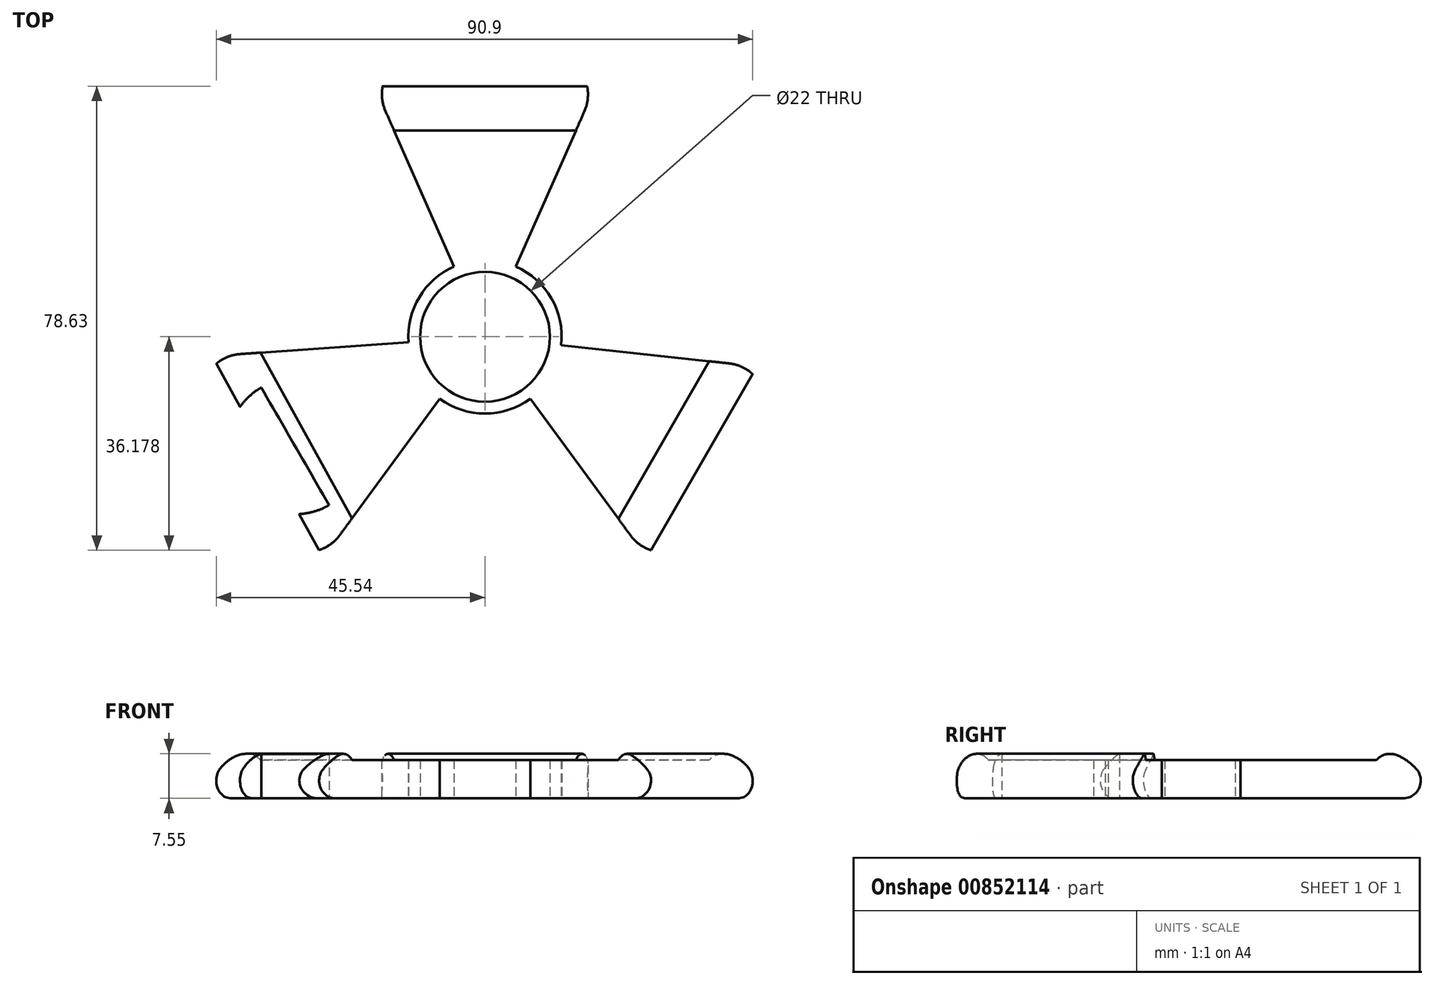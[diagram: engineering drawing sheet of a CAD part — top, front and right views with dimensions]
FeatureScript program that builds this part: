
annotation { "Feature Type Name" : "Feature", "Feature Type Description" : "" }
export const myFeature = defineFeature(function(context is Context, id is Id, definition is map)
    precondition{}
    {
        {
            var Q0;
            Q0=qCreatedBy(makeId("Top.planeOp"),FACE);
            var sketch = newSketch(context, id + "F0", { "sketchPlane" : qUnion([Q0])});
            skLineSegment(sketch, "E0", {"start": v(0, 55.7) * mm, "end": v(-32.16, 0) * mm});
            skLineSegment(sketch, "E1", {"start": v(-32.16, 0) * mm, "end": v(32.16, 0) * mm});
            skLineSegment(sketch, "E2", {"start": v(32.16, 0) * mm, "end": v(0, 55.7) * mm});
            skLineSegment(sketch, "E3", {"start": v(0, 55.7) * mm, "end": v(0, 0) * mm, "construction": true});
            skLineSegment(sketch, "E4", {"start": v(0, 0) * mm, "end": v(-32.16, 0) * mm, "construction": true});
            skLineSegment(sketch, "E5", {"start": v(-32.16, 0) * mm, "end": v(0, 18.57) * mm, "construction": true});
            skLineSegment(sketch, "E6", {"start": v(0, 18.57) * mm, "end": v(32.16, 0) * mm, "construction": true});
            skCircle(sketch, "E7", {"center": v(0, 18.57) * mm, "radius": 13 * mm});
            skCircle(sketch, "E8", {"center": v(-32.16, 0) * mm, "radius": 11.5 * mm});
            skCircle(sketch, "E9", {"center": v(0, 55.7) * mm, "radius": 6.79 * mm});
            skCircle(sketch, "E10", {"center": v(32.16, 0) * mm, "radius": 11.49 * mm});
            skLineSegment(sketch, "E11", {"start": v(0, 18.57) * mm, "end": v(-16.08, 27.85) * mm, "construction": true});
            skLineSegment(sketch, "E12", {"start": v(-16.08, 27.85) * mm, "end": v(0, 18.57) * mm, "construction": true});
            skLineSegment(sketch, "E13", {"start": v(0, 18.57) * mm, "end": v(16.08, 27.85) * mm, "construction": true});
            skLineSegment(sketch, "E14", {"start": v(6.79, 55.7) * mm, "end": v(-6.79, 55.7) * mm, "construction": true});
            skLineSegment(sketch, "E15", {"start": v(-20.66, 0) * mm, "end": v(-43.66, 0) * mm, "construction": true});
            skLineSegment(sketch, "E16", {"start": v(43.65, 0) * mm, "end": v(20.67, 0) * mm, "construction": true});
            skLineSegment(sketch, "E17", {"start": v(32.16, 0) * mm, "end": v(37.9, 9.95) * mm, "construction": true});
            skLineSegment(sketch, "E18", {"start": v(37.9, 9.95) * mm, "end": v(26.42, -9.95) * mm, "construction": true});
            skLineSegment(sketch, "E19", {"start": v(-32.16, 0) * mm, "end": v(-37.91, 9.96) * mm, "construction": true});
            skLineSegment(sketch, "E20", {"start": v(-37.91, 9.96) * mm, "end": v(-32.16, 0) * mm, "construction": true});
            skLineSegment(sketch, "E21", {"start": v(-32.16, 0) * mm, "end": v(-26.41, -9.96) * mm, "construction": true});
            skLineSegment(sketch, "E22", {"start": v(-26.41, -9.96) * mm, "end": v(0, 18.57) * mm});
            skLineSegment(sketch, "E23", {"start": v(-37.91, 9.96) * mm, "end": v(0, 18.57) * mm});
            skLineSegment(sketch, "E24", {"start": v(-6.79, 55.7) * mm, "end": v(0, 18.57) * mm});
            skLineSegment(sketch, "E25", {"start": v(6.79, 55.7) * mm, "end": v(0, 18.57) * mm});
            skLineSegment(sketch, "E26", {"start": v(26.42, -9.95) * mm, "end": v(0, 18.57) * mm});
            skLineSegment(sketch, "E27", {"start": v(37.9, 9.95) * mm, "end": v(0, 18.57) * mm});
            skLineSegment(sketch, "E28", {"start": v(32.16, 0) * mm, "end": v(41.84, 16.76) * mm});
            skLineSegment(sketch, "E29", {"start": v(41.84, 16.76) * mm, "end": v(22.49, -16.76) * mm});
            skLineSegment(sketch, "E30", {"start": v(-37.91, 9.96) * mm, "end": v(-21.6, -18.3) * mm});
            skLineSegment(sketch, "E31", {"start": v(-21.6, -18.3) * mm, "end": v(-37.91, 9.96) * mm});
            skLineSegment(sketch, "E32", {"start": v(-37.91, 9.96) * mm, "end": v(-42.88, 18.57) * mm});
            skLineSegment(sketch, "E33", {"start": v(6.79, 55.7) * mm, "end": v(19.36, 55.7) * mm});
            skLineSegment(sketch, "E34", {"start": v(19.36, 55.7) * mm, "end": v(-19.36, 55.7) * mm});
            skLineSegment(sketch, "E35", {"start": v(-42.88, 18.57) * mm, "end": v(0, 18.57) * mm});
            skLineSegment(sketch, "E36", {"start": v(0, 18.57) * mm, "end": v(-19.36, 55.7) * mm});
            skLineSegment(sketch, "E37", {"start": v(0, 18.57) * mm, "end": v(19.36, 55.7) * mm});
            skLineSegment(sketch, "E38", {"start": v(0, 18.57) * mm, "end": v(41.84, 16.76) * mm});
            skLineSegment(sketch, "E39", {"start": v(0, 18.57) * mm, "end": v(22.49, -16.76) * mm});
            skLineSegment(sketch, "E40", {"start": v(0, 18.57) * mm, "end": v(-21.6, -18.3) * mm});
            skLineSegment(sketch, "E41", {"start": v(-22.2, 5.75) * mm, "end": v(-42.12, -5.75) * mm, "construction": true});
            skLineSegment(sketch, "E42", {"start": v(32.16, 0) * mm, "end": v(42.1, -5.74) * mm, "construction": true});
            skLineSegment(sketch, "E43", {"start": v(0, 55.7) * mm, "end": v(0, 62.49) * mm, "construction": true});
            skLineSegment(sketch, "E44", {"start": v(-19.36, 55.7) * mm, "end": v(-19.36, 62.49) * mm, "construction": true});
            skLineSegment(sketch, "E45", {"start": v(-19.36, 62.49) * mm, "end": v(0, 62.49) * mm, "construction": true});
            skLineSegment(sketch, "E46", {"start": v(19.36, 62.49) * mm, "end": v(19.36, 55.7) * mm, "construction": true});
            skLineSegment(sketch, "E47", {"start": v(19.36, 62.49) * mm, "end": v(0, 62.49) * mm, "construction": true});
            skLineSegment(sketch, "E48", {"start": v(-42.88, 18.57) * mm, "end": v(-47.88, 15.2) * mm, "construction": true});
            skLineSegment(sketch, "E49", {"start": v(-47.88, 15.2) * mm, "end": v(-42.12, -5.75) * mm, "construction": true});
            skLineSegment(sketch, "E50", {"start": v(-21.6, -18.3) * mm, "end": v(-28.36, -20.16) * mm, "construction": true});
            skLineSegment(sketch, "E51", {"start": v(-28.36, -20.16) * mm, "end": v(-42.12, -5.75) * mm, "construction": true});
            skLineSegment(sketch, "E52", {"start": v(22.49, -16.76) * mm, "end": v(28.37, -20.15) * mm, "construction": true});
            skLineSegment(sketch, "E53", {"start": v(28.37, -20.15) * mm, "end": v(42.1, -5.74) * mm, "construction": true});
            skLineSegment(sketch, "E54", {"start": v(41.84, 16.76) * mm, "end": v(47.72, 13.36) * mm, "construction": true});
            skLineSegment(sketch, "E55", {"start": v(47.72, 13.36) * mm, "end": v(42.1, -5.74) * mm, "construction": true});
            skLineSegment(sketch, "E56", {"start": v(-28.36, -20.16) * mm, "end": v(0, 18.57) * mm});
            skLineSegment(sketch, "E57", {"start": v(0, 18.57) * mm, "end": v(-47.88, 15.2) * mm});
            skLineSegment(sketch, "E58", {"start": v(0, 18.57) * mm, "end": v(28.37, -20.15) * mm});
            skLineSegment(sketch, "E59", {"start": v(47.72, 13.36) * mm, "end": v(0, 18.57) * mm});
            skLineSegment(sketch, "E60", {"start": v(0, 18.57) * mm, "end": v(-19.36, 62.49) * mm});
            skLineSegment(sketch, "E61", {"start": v(0, 18.57) * mm, "end": v(19.36, 62.49) * mm});
            skLineSegment(sketch, "E62", {"start": v(19.36, 62.49) * mm, "end": v(-19.36, 62.49) * mm});
            skLineSegment(sketch, "E63", {"start": v(-28.36, -20.16) * mm, "end": v(-47.88, 15.2) * mm});
            skLineSegment(sketch, "E64", {"start": v(47.72, 13.36) * mm, "end": v(28.37, -20.15) * mm});
            skCircle(sketch, "E65", {"center": v(0, 18.57) * mm, "radius": 11 * mm});
            skLineSegment(sketch, "E66", {"start": v(0, 18.57) * mm, "end": v(-42.12, -5.75) * mm, "construction": true});
            skLineSegment(sketch, "E67", {"start": v(-16.37, 55.7) * mm, "end": v(-17.76, 52.64) * mm});
            skLineSegment(sketch, "E68", {"start": v(-16.89, 62.49) * mm, "end": v(-18.24, 59.93) * mm});
            skLineSegment(sketch, "E69", {"start": v(18.24, 59.95) * mm, "end": v(16.86, 62.49) * mm});
            skLineSegment(sketch, "E70", {"start": v(-45.13, 15.39) * mm, "end": v(-46.62, 12.91) * mm});
            skLineSegment(sketch, "E71", {"start": v(-26.71, -17.91) * mm, "end": v(-29.6, -17.91) * mm});
            skLineSegment(sketch, "E72", {"start": v(46.4, 11.1) * mm, "end": v(45.06, 13.65) * mm});
            skPoint(sketch, "E73.startSnap0", {"position": v(25.43, -18.46) * mm});
            skLineSegment(sketch, "E74", {"start": v(29.64, -17.95) * mm, "end": v(26.75, -17.95) * mm});
            skSolve(sketch);
        }
        {
            var Q0;
            {var subQ0=sQuery(id+"F0.wireOp",EDGE,"E23");var subQ1=sQuery(id+"F0.wireOp",EDGE,"E8");var subQ3=makeQuery(id+"F0.imprint","INTERSECT",VERTEX,{"derivedFrom":[subQ1,subQ0]});Q0=makeQuery(id+"F0.imprint","IMPRINT",FACE,{"disambiguationData":[TD([[makeQuery(id+"F0.imprint","IMPRINT",EDGE,{"disambiguationData":[TD([[subQ3,-1.0]])],"derivedFrom":subQ1}),1.0]])]});}
            var Q1;
            {var subQ0=sQuery(id+"F0.wireOp",EDGE,"E31");var subQ4=makeQuery(id+"F0.imprint","INTERSECT",VERTEX,{"derivedFrom":[sQuery(id+"F0.wireOp",EDGE,"E0"),sQuery(id+"F0.wireOp",EDGE,"E1"),subQ0]});Q1=makeQuery(id+"F0.imprint","IMPRINT",FACE,{"disambiguationData":[TD([[makeQuery(id+"F0.imprint","IMPRINT",EDGE,{"disambiguationData":[TD([[subQ4,1.0]])],"derivedFrom":subQ0}),1.0]])]});}
            var Q2;
            {var subQ0=sQuery(id+"F0.wireOp",EDGE,"E22");var subQ1=sQuery(id+"F0.wireOp",EDGE,"E8");var subQ3=makeQuery(id+"F0.imprint","INTERSECT",VERTEX,{"derivedFrom":[subQ1,subQ0]});Q2=makeQuery(id+"F0.imprint","IMPRINT",FACE,{"disambiguationData":[TD([[makeQuery(id+"F0.imprint","IMPRINT",EDGE,{"disambiguationData":[TD([[subQ3,1.0]])],"derivedFrom":subQ1}),1.0]])]});}
            var Q3;
            {var subQ0=sQuery(id+"F0.wireOp",EDGE,"E34");var subQ1=sQuery(id+"F0.wireOp",EDGE,"E9");var subQ2=makeQuery(id+"F0.imprint","INTERSECT",VERTEX,{"derivedFrom":[subQ1,sQuery(id+"F0.wireOp",EDGE,"E24"),subQ0]});Q3=makeQuery(id+"F0.imprint","IMPRINT",FACE,{"disambiguationData":[TD([[makeQuery(id+"F0.imprint","IMPRINT",EDGE,{"disambiguationData":[TD([[subQ2,1.0]])],"derivedFrom":subQ1}),1.0]])]});}
            var Q4;
            {var subQ0=sQuery(id+"F0.wireOp",EDGE,"E24");var subQ1=sQuery(id+"F0.wireOp",EDGE,"E9");var subQ3=makeQuery(id+"F0.imprint","INTERSECT",VERTEX,{"derivedFrom":[subQ1,subQ0]});Q4=makeQuery(id+"F0.imprint","IMPRINT",FACE,{"disambiguationData":[TD([[makeQuery(id+"F0.imprint","IMPRINT",EDGE,{"disambiguationData":[TD([[subQ3,1.0]])],"derivedFrom":subQ1}),1.0]])]});}
            var Q5;
            {var subQ0=sQuery(id+"F0.wireOp",EDGE,"E25");var subQ1=sQuery(id+"F0.wireOp",EDGE,"E9");var subQ3=makeQuery(id+"F0.imprint","INTERSECT",VERTEX,{"derivedFrom":[subQ1,subQ0]});Q5=makeQuery(id+"F0.imprint","IMPRINT",FACE,{"disambiguationData":[TD([[makeQuery(id+"F0.imprint","IMPRINT",EDGE,{"disambiguationData":[TD([[subQ3,-1.0]])],"derivedFrom":subQ1}),1.0]])]});}
            var Q6;
            {var subQ0=sQuery(id+"F0.wireOp",EDGE,"E27");var subQ1=sQuery(id+"F0.wireOp",EDGE,"E10");var subQ3=makeQuery(id+"F0.imprint","INTERSECT",VERTEX,{"derivedFrom":[subQ1,subQ0]});Q6=makeQuery(id+"F0.imprint","IMPRINT",FACE,{"disambiguationData":[TD([[makeQuery(id+"F0.imprint","IMPRINT",EDGE,{"disambiguationData":[TD([[subQ3,1.0]])],"derivedFrom":subQ1}),1.0]])]});}
            var Q7;
            {var subQ0=sQuery(id+"F0.wireOp",EDGE,"E26");var subQ1=sQuery(id+"F0.wireOp",EDGE,"E10");var subQ3=makeQuery(id+"F0.imprint","INTERSECT",VERTEX,{"derivedFrom":[subQ1,subQ0]});Q7=makeQuery(id+"F0.imprint","IMPRINT",FACE,{"disambiguationData":[TD([[makeQuery(id+"F0.imprint","IMPRINT",EDGE,{"disambiguationData":[TD([[subQ3,-1.0]])],"derivedFrom":subQ1}),1.0]])]});}
            var Q8;
            {var subQ0=sQuery(id+"F0.wireOp",EDGE,"E29");var subQ1=sQuery(id+"F0.wireOp",EDGE,"E10");var subQ2=makeQuery(id+"F0.imprint","INTERSECT",VERTEX,{"derivedFrom":[subQ1,sQuery(id+"F0.wireOp",EDGE,"E26"),subQ0]});Q8=makeQuery(id+"F0.imprint","IMPRINT",FACE,{"disambiguationData":[TD([[makeQuery(id+"F0.imprint","IMPRINT",EDGE,{"disambiguationData":[TD([[subQ2,-1.0]])],"derivedFrom":subQ1}),1.0]])]});}
            var Q9;
            {var subQ1=sQuery(id+"F0.wireOp",EDGE,"E0");var subQ3=sQuery(id+"F0.wireOp",EDGE,"E9");var subQ4=makeQuery(id+"F0.imprint","INTERSECT",VERTEX,{"derivedFrom":[subQ1,subQ3]});Q9=makeQuery(id+"F0.imprint","IMPRINT",FACE,{"disambiguationData":[TD([[makeQuery(id+"F0.imprint","IMPRINT",EDGE,{"disambiguationData":[TD([[subQ4,1.0]])],"derivedFrom":subQ3}),1.0]])]});}
            var Q10;
            {var subQ1=sQuery(id+"F0.wireOp",EDGE,"E0");var subQ3=sQuery(id+"F0.wireOp",EDGE,"E8");var subQ4=makeQuery(id+"F0.imprint","INTERSECT",VERTEX,{"derivedFrom":[subQ1,subQ3]});Q10=makeQuery(id+"F0.imprint","IMPRINT",FACE,{"disambiguationData":[TD([[makeQuery(id+"F0.imprint","IMPRINT",EDGE,{"disambiguationData":[TD([[subQ4,-1.0]])],"derivedFrom":subQ3}),1.0]])]});}
            var Q11;
            {var subQ1=sQuery(id+"F0.wireOp",EDGE,"E1");var subQ3=sQuery(id+"F0.wireOp",EDGE,"E8");var subQ4=makeQuery(id+"F0.imprint","INTERSECT",VERTEX,{"derivedFrom":[subQ1,subQ3]});Q11=makeQuery(id+"F0.imprint","IMPRINT",FACE,{"disambiguationData":[TD([[makeQuery(id+"F0.imprint","IMPRINT",EDGE,{"disambiguationData":[TD([[subQ4,1.0]])],"derivedFrom":subQ3}),1.0]])]});}
            var Q12;
            {var subQ1=sQuery(id+"F0.wireOp",EDGE,"E1");var subQ3=sQuery(id+"F0.wireOp",EDGE,"E10");var subQ4=makeQuery(id+"F0.imprint","INTERSECT",VERTEX,{"derivedFrom":[subQ1,subQ3]});Q12=makeQuery(id+"F0.imprint","IMPRINT",FACE,{"disambiguationData":[TD([[makeQuery(id+"F0.imprint","IMPRINT",EDGE,{"disambiguationData":[TD([[subQ4,-1.0]])],"derivedFrom":subQ3}),1.0]])]});}
            var Q13;
            {var subQ1=sQuery(id+"F0.wireOp",EDGE,"E2");var subQ3=sQuery(id+"F0.wireOp",EDGE,"E10");var subQ4=makeQuery(id+"F0.imprint","INTERSECT",VERTEX,{"derivedFrom":[subQ1,subQ3]});Q13=makeQuery(id+"F0.imprint","IMPRINT",FACE,{"disambiguationData":[TD([[makeQuery(id+"F0.imprint","IMPRINT",EDGE,{"disambiguationData":[TD([[subQ4,1.0]])],"derivedFrom":subQ3}),1.0]])]});}
            var Q14;
            {var subQ1=sQuery(id+"F0.wireOp",EDGE,"E2");var subQ3=sQuery(id+"F0.wireOp",EDGE,"E9");var subQ4=makeQuery(id+"F0.imprint","INTERSECT",VERTEX,{"derivedFrom":[subQ1,subQ3]});Q14=makeQuery(id+"F0.imprint","IMPRINT",FACE,{"disambiguationData":[TD([[makeQuery(id+"F0.imprint","IMPRINT",EDGE,{"disambiguationData":[TD([[subQ4,-1.0]])],"derivedFrom":subQ3}),1.0]])]});}
            var Q15;
            {var subQ1=sQuery(id+"F0.wireOp",EDGE,"E0");var subQ3=sQuery(id+"F0.wireOp",EDGE,"E8");var subQ4=makeQuery(id+"F0.imprint","INTERSECT",VERTEX,{"derivedFrom":[subQ1,subQ3]});Q15=makeQuery(id+"F0.imprint","IMPRINT",FACE,{"disambiguationData":[TD([[makeQuery(id+"F0.imprint","IMPRINT",EDGE,{"disambiguationData":[TD([[subQ4,1.0]])],"derivedFrom":subQ3}),1.0]])]});}
            var Q16;
            {var subQ0=sQuery(id+"F0.wireOp",EDGE,"E23");var subQ6=sQuery(id+"F0.wireOp",EDGE,"E0");var subQ11=makeQuery(id+"F0.imprint","INTERSECT",VERTEX,{"derivedFrom":[subQ6,subQ0]});Q16=makeQuery(id+"F0.imprint","IMPRINT",FACE,{"disambiguationData":[TD([[makeQuery(id+"F0.imprint","IMPRINT",EDGE,{"disambiguationData":[TD([[subQ11,-1.0]])],"derivedFrom":subQ6}),1.0]])]});}
            var Q17;
            {var subQ0=sQuery(id+"F0.wireOp",EDGE,"E23");var subQ1=sQuery(id+"F0.wireOp",EDGE,"E0");var subQ2=makeQuery(id+"F0.imprint","INTERSECT",VERTEX,{"derivedFrom":[subQ1,subQ0]});Q17=makeQuery(id+"F0.imprint","IMPRINT",FACE,{"disambiguationData":[TD([[makeQuery(id+"F0.imprint","IMPRINT",EDGE,{"disambiguationData":[TD([[subQ2,-1.0]])],"derivedFrom":subQ1}),-1.0]])]});}
            var Q18;
            {var subQ0=sQuery(id+"F0.wireOp",EDGE,"E8");var subQ1=sQuery(id+"F0.wireOp",EDGE,"E1");var subQ2=makeQuery(id+"F0.imprint","INTERSECT",VERTEX,{"derivedFrom":[subQ1,subQ0]});Q18=makeQuery(id+"F0.imprint","IMPRINT",FACE,{"disambiguationData":[TD([[makeQuery(id+"F0.imprint","IMPRINT",EDGE,{"disambiguationData":[TD([[subQ2,-1.0]])],"derivedFrom":subQ1}),-1.0]])]});}
            var Q19;
            {var subQ0=sQuery(id+"F0.wireOp",EDGE,"E26");var subQ9=sQuery(id+"F0.wireOp",EDGE,"E1");var subQ11=makeQuery(id+"F0.imprint","INTERSECT",VERTEX,{"derivedFrom":[subQ9,subQ0]});Q19=makeQuery(id+"F0.imprint","IMPRINT",FACE,{"disambiguationData":[TD([[makeQuery(id+"F0.imprint","IMPRINT",EDGE,{"disambiguationData":[TD([[subQ11,-1.0]])],"derivedFrom":subQ9}),1.0]])]});}
            var Q20;
            {var subQ1=sQuery(id+"F0.wireOp",EDGE,"E1");var subQ3=sQuery(id+"F0.wireOp",EDGE,"E10");var subQ4=makeQuery(id+"F0.imprint","INTERSECT",VERTEX,{"derivedFrom":[subQ1,subQ3]});Q20=makeQuery(id+"F0.imprint","IMPRINT",FACE,{"disambiguationData":[TD([[makeQuery(id+"F0.imprint","IMPRINT",EDGE,{"disambiguationData":[TD([[subQ4,1.0]])],"derivedFrom":subQ3}),1.0]])]});}
            var Q21;
            {var subQ0=sQuery(id+"F0.wireOp",EDGE,"E26");var subQ1=sQuery(id+"F0.wireOp",EDGE,"E1");var subQ2=makeQuery(id+"F0.imprint","INTERSECT",VERTEX,{"derivedFrom":[subQ1,subQ0]});Q21=makeQuery(id+"F0.imprint","IMPRINT",FACE,{"disambiguationData":[TD([[makeQuery(id+"F0.imprint","IMPRINT",EDGE,{"disambiguationData":[TD([[subQ2,-1.0]])],"derivedFrom":subQ1}),-1.0]])]});}
            var Q22;
            {var subQ0=sQuery(id+"F0.wireOp",EDGE,"E10");var subQ1=sQuery(id+"F0.wireOp",EDGE,"E2");var subQ2=makeQuery(id+"F0.imprint","INTERSECT",VERTEX,{"derivedFrom":[subQ1,subQ0]});Q22=makeQuery(id+"F0.imprint","IMPRINT",FACE,{"disambiguationData":[TD([[makeQuery(id+"F0.imprint","IMPRINT",EDGE,{"disambiguationData":[TD([[subQ2,-1.0]])],"derivedFrom":subQ1}),-1.0]])]});}
            var Q23;
            {var subQ1=sQuery(id+"F0.wireOp",EDGE,"E0");var subQ3=sQuery(id+"F0.wireOp",EDGE,"E9");var subQ4=makeQuery(id+"F0.imprint","INTERSECT",VERTEX,{"derivedFrom":[subQ1,subQ3]});Q23=makeQuery(id+"F0.imprint","IMPRINT",FACE,{"disambiguationData":[TD([[makeQuery(id+"F0.imprint","IMPRINT",EDGE,{"disambiguationData":[TD([[subQ4,-1.0]])],"derivedFrom":subQ3}),1.0]])]});}
            var Q24;
            {var subQ0=sQuery(id+"F0.wireOp",EDGE,"E25");var subQ1=sQuery(id+"F0.wireOp",EDGE,"E2");var subQ2=makeQuery(id+"F0.imprint","INTERSECT",VERTEX,{"derivedFrom":[subQ1,subQ0]});Q24=makeQuery(id+"F0.imprint","IMPRINT",FACE,{"disambiguationData":[TD([[makeQuery(id+"F0.imprint","IMPRINT",EDGE,{"disambiguationData":[TD([[subQ2,-1.0]])],"derivedFrom":subQ1}),-1.0]])]});}
            var Q25;
            {var subQ0=sQuery(id+"F0.wireOp",EDGE,"E9");var subQ1=sQuery(id+"F0.wireOp",EDGE,"E0");var subQ2=makeQuery(id+"F0.imprint","INTERSECT",VERTEX,{"derivedFrom":[subQ1,subQ0]});Q25=makeQuery(id+"F0.imprint","IMPRINT",FACE,{"disambiguationData":[TD([[makeQuery(id+"F0.imprint","IMPRINT",EDGE,{"disambiguationData":[TD([[subQ2,-1.0]])],"derivedFrom":subQ1}),-1.0]])]});}
            var Q26;
            {var subQ0=sQuery(id+"F0.wireOp",EDGE,"E9");var subQ1=sQuery(id+"F0.wireOp",EDGE,"E0");var subQ2=makeQuery(id+"F0.imprint","INTERSECT",VERTEX,{"derivedFrom":[subQ1,subQ0]});Q26=makeQuery(id+"F0.imprint","IMPRINT",FACE,{"disambiguationData":[TD([[makeQuery(id+"F0.imprint","IMPRINT",EDGE,{"disambiguationData":[TD([[subQ2,-1.0]])],"derivedFrom":subQ1}),1.0]])]});}
            var Q27;
            {var subQ0=sQuery(id+"F0.wireOp",EDGE,"E25");var subQ1=sQuery(id+"F0.wireOp",EDGE,"E7");var subQ2=makeQuery(id+"F0.imprint","INTERSECT",VERTEX,{"derivedFrom":[subQ1,subQ0]});Q27=makeQuery(id+"F0.imprint","IMPRINT",FACE,{"disambiguationData":[TD([[makeQuery(id+"F0.imprint","IMPRINT",EDGE,{"disambiguationData":[TD([[subQ2,1.0]])],"derivedFrom":subQ1}),1.0]])]});}
            var Q28;
            {var subQ0=sQuery(id+"F0.wireOp",EDGE,"E25");var subQ1=sQuery(id+"F0.wireOp",EDGE,"E7");var subQ2=makeQuery(id+"F0.imprint","INTERSECT",VERTEX,{"derivedFrom":[subQ1,subQ0]});Q28=makeQuery(id+"F0.imprint","IMPRINT",FACE,{"disambiguationData":[TD([[makeQuery(id+"F0.imprint","IMPRINT",EDGE,{"disambiguationData":[TD([[subQ2,-1.0]])],"derivedFrom":subQ1}),1.0]])]});}
            var Q29;
            {var subQ0=sQuery(id+"F0.wireOp",EDGE,"E24");var subQ1=sQuery(id+"F0.wireOp",EDGE,"E7");var subQ2=makeQuery(id+"F0.imprint","INTERSECT",VERTEX,{"derivedFrom":[subQ1,subQ0]});Q29=makeQuery(id+"F0.imprint","IMPRINT",FACE,{"disambiguationData":[TD([[makeQuery(id+"F0.imprint","IMPRINT",EDGE,{"disambiguationData":[TD([[subQ2,-1.0]])],"derivedFrom":subQ1}),1.0]])]});}
            var Q30;
            {var subQ0=sQuery(id+"F0.wireOp",EDGE,"E23");var subQ1=sQuery(id+"F0.wireOp",EDGE,"E7");var subQ2=makeQuery(id+"F0.imprint","INTERSECT",VERTEX,{"derivedFrom":[subQ1,subQ0]});Q30=makeQuery(id+"F0.imprint","IMPRINT",FACE,{"disambiguationData":[TD([[makeQuery(id+"F0.imprint","IMPRINT",EDGE,{"disambiguationData":[TD([[subQ2,-1.0]])],"derivedFrom":subQ1}),1.0]])]});}
            var Q31;
            {var subQ0=sQuery(id+"F0.wireOp",EDGE,"E22");var subQ1=sQuery(id+"F0.wireOp",EDGE,"E7");var subQ2=makeQuery(id+"F0.imprint","INTERSECT",VERTEX,{"derivedFrom":[subQ1,subQ0]});Q31=makeQuery(id+"F0.imprint","IMPRINT",FACE,{"disambiguationData":[TD([[makeQuery(id+"F0.imprint","IMPRINT",EDGE,{"disambiguationData":[TD([[subQ2,-1.0]])],"derivedFrom":subQ1}),1.0]])]});}
            var Q32;
            {var subQ0=sQuery(id+"F0.wireOp",EDGE,"E26");var subQ1=sQuery(id+"F0.wireOp",EDGE,"E7");var subQ2=makeQuery(id+"F0.imprint","INTERSECT",VERTEX,{"derivedFrom":[subQ1,subQ0]});Q32=makeQuery(id+"F0.imprint","IMPRINT",FACE,{"disambiguationData":[TD([[makeQuery(id+"F0.imprint","IMPRINT",EDGE,{"disambiguationData":[TD([[subQ2,-1.0]])],"derivedFrom":subQ1}),1.0]])]});}
            var Q33;
            {var subQ0=sQuery(id+"F0.wireOp",EDGE,"E27");var subQ1=sQuery(id+"F0.wireOp",EDGE,"E7");var subQ2=makeQuery(id+"F0.imprint","INTERSECT",VERTEX,{"derivedFrom":[subQ1,subQ0]});Q33=makeQuery(id+"F0.imprint","IMPRINT",FACE,{"disambiguationData":[TD([[makeQuery(id+"F0.imprint","IMPRINT",EDGE,{"disambiguationData":[TD([[subQ2,-1.0]])],"derivedFrom":subQ1}),1.0]])]});}
            var Q34;
            {var subQ1=sQuery(id+"F0.wireOp",EDGE,"E22");var subQ6=sQuery(id+"F0.wireOp",EDGE,"E1");var subQ7=makeQuery(id+"F0.imprint","INTERSECT",VERTEX,{"derivedFrom":[subQ6,subQ1]});Q34=makeQuery(id+"F0.imprint","IMPRINT",FACE,{"disambiguationData":[TD([[makeQuery(id+"F0.imprint","IMPRINT",EDGE,{"disambiguationData":[TD([[subQ7,-1.0]])],"derivedFrom":subQ6}),-1.0]])]});}
            var Q35;
            {var subQ0=sQuery(id+"F0.wireOp",EDGE,"E22");var subQ1=sQuery(id+"F0.wireOp",EDGE,"E1");var subQ2=makeQuery(id+"F0.imprint","INTERSECT",VERTEX,{"derivedFrom":[subQ1,subQ0]});Q35=makeQuery(id+"F0.imprint","IMPRINT",FACE,{"disambiguationData":[TD([[makeQuery(id+"F0.imprint","IMPRINT",EDGE,{"disambiguationData":[TD([[subQ2,-1.0]])],"derivedFrom":subQ1}),1.0]])]});}
            var Q36;
            {var subQ4=sQuery(id+"F0.wireOp",EDGE,"E57");var subQ7=sQuery(id+"F0.wireOp",EDGE,"E0");var subQ9=makeQuery(id+"F0.imprint","INTERSECT",VERTEX,{"derivedFrom":[subQ7,subQ4]});Q36=makeQuery(id+"F0.imprint","IMPRINT",FACE,{"disambiguationData":[TD([[makeQuery(id+"F0.imprint","IMPRINT",EDGE,{"disambiguationData":[TD([[subQ9,-1.0]])],"derivedFrom":subQ7}),-1.0]])]});}
            var Q37;
            {var subQ1=sQuery(id+"F0.wireOp",EDGE,"E1");var subQ7=sQuery(id+"F0.wireOp",EDGE,"E58");var subQ9=makeQuery(id+"F0.imprint","INTERSECT",VERTEX,{"derivedFrom":[subQ1,subQ7]});Q37=makeQuery(id+"F0.imprint","IMPRINT",FACE,{"disambiguationData":[TD([[makeQuery(id+"F0.imprint","IMPRINT",EDGE,{"disambiguationData":[TD([[subQ9,-1.0]])],"derivedFrom":subQ1}),-1.0]])]});}
            var Q38;
            {var subQ1=sQuery(id+"F0.wireOp",EDGE,"E27");var subQ6=sQuery(id+"F0.wireOp",EDGE,"E2");var subQ7=makeQuery(id+"F0.imprint","INTERSECT",VERTEX,{"derivedFrom":[subQ6,subQ1]});Q38=makeQuery(id+"F0.imprint","IMPRINT",FACE,{"disambiguationData":[TD([[makeQuery(id+"F0.imprint","IMPRINT",EDGE,{"disambiguationData":[TD([[subQ7,-1.0]])],"derivedFrom":subQ6}),-1.0]])]});}
            var Q39;
            {var subQ0=sQuery(id+"F0.wireOp",EDGE,"E61");var subQ1=sQuery(id+"F0.wireOp",EDGE,"E2");var subQ2=makeQuery(id+"F0.imprint","INTERSECT",VERTEX,{"derivedFrom":[subQ1,subQ0]});Q39=makeQuery(id+"F0.imprint","IMPRINT",FACE,{"disambiguationData":[TD([[makeQuery(id+"F0.imprint","IMPRINT",EDGE,{"disambiguationData":[TD([[subQ2,-1.0]])],"derivedFrom":subQ1}),1.0]])]});}
            var Q40;
            {var subQ0=sQuery(id+"F0.wireOp",EDGE,"E24");var subQ1=sQuery(id+"F0.wireOp",EDGE,"E0");var subQ2=makeQuery(id+"F0.imprint","INTERSECT",VERTEX,{"derivedFrom":[subQ1,subQ0]});Q40=makeQuery(id+"F0.imprint","IMPRINT",FACE,{"disambiguationData":[TD([[makeQuery(id+"F0.imprint","IMPRINT",EDGE,{"disambiguationData":[TD([[subQ2,-1.0]])],"derivedFrom":subQ1}),1.0]])]});}
            var Q41;
            {var subQ1=sQuery(id+"F0.wireOp",EDGE,"E24");var subQ6=sQuery(id+"F0.wireOp",EDGE,"E0");var subQ7=makeQuery(id+"F0.imprint","INTERSECT",VERTEX,{"derivedFrom":[subQ6,subQ1]});Q41=makeQuery(id+"F0.imprint","IMPRINT",FACE,{"disambiguationData":[TD([[makeQuery(id+"F0.imprint","IMPRINT",EDGE,{"disambiguationData":[TD([[subQ7,-1.0]])],"derivedFrom":subQ6}),-1.0]])]});}
            var Q42;
            {var subQ4=sQuery(id+"F0.wireOp",EDGE,"E61");var subQ7=sQuery(id+"F0.wireOp",EDGE,"E2");var subQ9=makeQuery(id+"F0.imprint","INTERSECT",VERTEX,{"derivedFrom":[subQ7,subQ4]});Q42=makeQuery(id+"F0.imprint","IMPRINT",FACE,{"disambiguationData":[TD([[makeQuery(id+"F0.imprint","IMPRINT",EDGE,{"disambiguationData":[TD([[subQ9,-1.0]])],"derivedFrom":subQ7}),-1.0]])]});}
            var Q43;
            {var subQ0=sQuery(id+"F0.wireOp",EDGE,"E27");var subQ1=sQuery(id+"F0.wireOp",EDGE,"E2");var subQ2=makeQuery(id+"F0.imprint","INTERSECT",VERTEX,{"derivedFrom":[subQ1,subQ0]});Q43=makeQuery(id+"F0.imprint","IMPRINT",FACE,{"disambiguationData":[TD([[makeQuery(id+"F0.imprint","IMPRINT",EDGE,{"disambiguationData":[TD([[subQ2,-1.0]])],"derivedFrom":subQ1}),1.0]])]});}
            var Q44;
            {var subQ0=sQuery(id+"F0.wireOp",EDGE,"E58");var subQ1=sQuery(id+"F0.wireOp",EDGE,"E1");var subQ2=makeQuery(id+"F0.imprint","INTERSECT",VERTEX,{"derivedFrom":[subQ1,subQ0]});Q44=makeQuery(id+"F0.imprint","IMPRINT",FACE,{"disambiguationData":[TD([[makeQuery(id+"F0.imprint","IMPRINT",EDGE,{"disambiguationData":[TD([[subQ2,-1.0]])],"derivedFrom":subQ1}),1.0]])]});}
            var Q45;
            {var subQ0=sQuery(id+"F0.wireOp",EDGE,"E57");var subQ1=sQuery(id+"F0.wireOp",EDGE,"E0");var subQ2=makeQuery(id+"F0.imprint","INTERSECT",VERTEX,{"derivedFrom":[subQ1,subQ0]});Q45=makeQuery(id+"F0.imprint","IMPRINT",FACE,{"disambiguationData":[TD([[makeQuery(id+"F0.imprint","IMPRINT",EDGE,{"disambiguationData":[TD([[subQ2,-1.0]])],"derivedFrom":subQ1}),1.0]])]});}
            var Q46;
            {var subQ0=sQuery(id+"F0.wireOp",EDGE,"E57");var subQ1=sQuery(id+"F0.wireOp",EDGE,"E7");var subQ2=makeQuery(id+"F0.imprint","INTERSECT",VERTEX,{"derivedFrom":[subQ1,subQ0]});Q46=makeQuery(id+"F0.imprint","IMPRINT",FACE,{"disambiguationData":[TD([[makeQuery(id+"F0.imprint","IMPRINT",EDGE,{"disambiguationData":[TD([[subQ2,-1.0]])],"derivedFrom":subQ1}),1.0]])]});}
            var Q47;
            {var subQ0=sQuery(id+"F0.wireOp",EDGE,"E40");var subQ1=sQuery(id+"F0.wireOp",EDGE,"E7");var subQ2=makeQuery(id+"F0.imprint","INTERSECT",VERTEX,{"derivedFrom":[subQ1,subQ0]});Q47=makeQuery(id+"F0.imprint","IMPRINT",FACE,{"disambiguationData":[TD([[makeQuery(id+"F0.imprint","IMPRINT",EDGE,{"disambiguationData":[TD([[subQ2,-1.0]])],"derivedFrom":subQ1}),1.0]])]});}
            var Q48;
            {var subQ0=sQuery(id+"F0.wireOp",EDGE,"E37");var subQ1=sQuery(id+"F0.wireOp",EDGE,"E7");var subQ2=makeQuery(id+"F0.imprint","INTERSECT",VERTEX,{"derivedFrom":[subQ1,subQ0]});Q48=makeQuery(id+"F0.imprint","IMPRINT",FACE,{"disambiguationData":[TD([[makeQuery(id+"F0.imprint","IMPRINT",EDGE,{"disambiguationData":[TD([[subQ2,1.0]])],"derivedFrom":subQ1}),1.0]])]});}
            var Q49;
            {var subQ0=sQuery(id+"F0.wireOp",EDGE,"E36");var subQ1=sQuery(id+"F0.wireOp",EDGE,"E7");var subQ2=makeQuery(id+"F0.imprint","INTERSECT",VERTEX,{"derivedFrom":[subQ1,subQ0]});Q49=makeQuery(id+"F0.imprint","IMPRINT",FACE,{"disambiguationData":[TD([[makeQuery(id+"F0.imprint","IMPRINT",EDGE,{"disambiguationData":[TD([[subQ2,-1.0]])],"derivedFrom":subQ1}),1.0]])]});}
            var Q50;
            {var subQ0=sQuery(id+"F0.wireOp",EDGE,"E35");var subQ1=sQuery(id+"F0.wireOp",EDGE,"E7");var subQ2=makeQuery(id+"F0.imprint","INTERSECT",VERTEX,{"derivedFrom":[subQ1,subQ0]});Q50=makeQuery(id+"F0.imprint","IMPRINT",FACE,{"disambiguationData":[TD([[makeQuery(id+"F0.imprint","IMPRINT",EDGE,{"disambiguationData":[TD([[subQ2,-1.0]])],"derivedFrom":subQ1}),1.0]])]});}
            var Q51;
            {var subQ0=sQuery(id+"F0.wireOp",EDGE,"E56");var subQ1=sQuery(id+"F0.wireOp",EDGE,"E7");var subQ2=makeQuery(id+"F0.imprint","INTERSECT",VERTEX,{"derivedFrom":[subQ1,subQ0]});Q51=makeQuery(id+"F0.imprint","IMPRINT",FACE,{"disambiguationData":[TD([[makeQuery(id+"F0.imprint","IMPRINT",EDGE,{"disambiguationData":[TD([[subQ2,-1.0]])],"derivedFrom":subQ1}),1.0]])]});}
            var Q52;
            {var subQ0=sQuery(id+"F0.wireOp",EDGE,"E59");var subQ1=sQuery(id+"F0.wireOp",EDGE,"E7");var subQ2=makeQuery(id+"F0.imprint","INTERSECT",VERTEX,{"derivedFrom":[subQ1,subQ0]});Q52=makeQuery(id+"F0.imprint","IMPRINT",FACE,{"disambiguationData":[TD([[makeQuery(id+"F0.imprint","IMPRINT",EDGE,{"disambiguationData":[TD([[subQ2,-1.0]])],"derivedFrom":subQ1}),1.0]])]});}
            var Q53;
            {var subQ0=sQuery(id+"F0.wireOp",EDGE,"E61");var subQ1=sQuery(id+"F0.wireOp",EDGE,"E7");var subQ2=makeQuery(id+"F0.imprint","INTERSECT",VERTEX,{"derivedFrom":[subQ1,subQ0]});Q53=makeQuery(id+"F0.imprint","IMPRINT",FACE,{"disambiguationData":[TD([[makeQuery(id+"F0.imprint","IMPRINT",EDGE,{"disambiguationData":[TD([[subQ2,1.0]])],"derivedFrom":subQ1}),1.0]])]});}
            var Q54;
            {var subQ0=sQuery(id+"F0.wireOp",EDGE,"E58");var subQ1=sQuery(id+"F0.wireOp",EDGE,"E7");var subQ2=makeQuery(id+"F0.imprint","INTERSECT",VERTEX,{"derivedFrom":[subQ1,subQ0]});Q54=makeQuery(id+"F0.imprint","IMPRINT",FACE,{"disambiguationData":[TD([[makeQuery(id+"F0.imprint","IMPRINT",EDGE,{"disambiguationData":[TD([[subQ2,-1.0]])],"derivedFrom":subQ1}),1.0]])]});}
            var Q55;
            {var subQ0=sQuery(id+"F0.wireOp",EDGE,"E39");var subQ1=sQuery(id+"F0.wireOp",EDGE,"E7");var subQ2=makeQuery(id+"F0.imprint","INTERSECT",VERTEX,{"derivedFrom":[subQ1,subQ0]});Q55=makeQuery(id+"F0.imprint","IMPRINT",FACE,{"disambiguationData":[TD([[makeQuery(id+"F0.imprint","IMPRINT",EDGE,{"disambiguationData":[TD([[subQ2,-1.0]])],"derivedFrom":subQ1}),1.0]])]});}
            var Q56;
            {var subQ0=sQuery(id+"F0.wireOp",EDGE,"E60");var subQ1=sQuery(id+"F0.wireOp",EDGE,"E7");var subQ2=makeQuery(id+"F0.imprint","INTERSECT",VERTEX,{"derivedFrom":[subQ1,subQ0]});Q56=makeQuery(id+"F0.imprint","IMPRINT",FACE,{"disambiguationData":[TD([[makeQuery(id+"F0.imprint","IMPRINT",EDGE,{"disambiguationData":[TD([[subQ2,-1.0]])],"derivedFrom":subQ1}),1.0]])]});}
            var Q57;
            {var subQ0=sQuery(id+"F0.wireOp",EDGE,"E68");Q57=makeQuery(id+"F0.imprint","IMPRINT",FACE,{"disambiguationData":[TD([[makeQuery(id+"F0.imprint","IMPRINT",EDGE,{"derivedFrom":subQ0}),1.0]])]});}
            var Q58;
            {var subQ0=sQuery(id+"F0.wireOp",EDGE,"E70");Q58=makeQuery(id+"F0.imprint","IMPRINT",FACE,{"disambiguationData":[TD([[makeQuery(id+"F0.imprint","IMPRINT",EDGE,{"derivedFrom":subQ0}),1.0]])]});}
            var Q59;
            {var subQ0=sQuery(id+"F0.wireOp",EDGE,"E71");Q59=makeQuery(id+"F0.imprint","IMPRINT",FACE,{"disambiguationData":[TD([[makeQuery(id+"F0.imprint","IMPRINT",EDGE,{"derivedFrom":subQ0}),-1.0]])]});}
            var Q60;
            {var subQ0=sQuery(id+"F0.wireOp",EDGE,"E72");Q60=makeQuery(id+"F0.imprint","IMPRINT",FACE,{"disambiguationData":[TD([[makeQuery(id+"F0.imprint","IMPRINT",EDGE,{"derivedFrom":subQ0}),1.0]])]});}
            var Q61;
            {var subQ0=sQuery(id+"F0.wireOp",EDGE,"E74");Q61=makeQuery(id+"F0.imprint","IMPRINT",FACE,{"disambiguationData":[TD([[makeQuery(id+"F0.imprint","IMPRINT",EDGE,{"derivedFrom":subQ0}),-1.0]])]});}
            var Q62;
            {var subQ0=sQuery(id+"F0.wireOp",EDGE,"E69");Q62=makeQuery(id+"F0.imprint","IMPRINT",FACE,{"disambiguationData":[TD([[makeQuery(id+"F0.imprint","IMPRINT",EDGE,{"derivedFrom":subQ0}),1.0]])]});}
            extrude(context, id + "F1", {"entities" : qUnion([Q0, Q1, Q2, Q3, Q4, Q5, Q6, Q7, Q8, Q9, Q10, Q11, Q12, Q13, Q14, Q15, Q16, Q17, Q18, Q19, Q20, Q21, Q22, Q23, Q24, Q25, Q26, Q27, Q28, Q29, Q30, Q31, Q32, Q33, Q34, Q35, Q36, Q37, Q38, Q39, Q40, Q41, Q42, Q43, Q44, Q45, Q46, Q47, Q48, Q49, Q50, Q51, Q52, Q53, Q54, Q55, Q56, Q57, Q58, Q59, Q60, Q61, Q62]), "depth" : 8 * mm, "offsetDistance" : 25 * mm});
        }
        {
            var Q0;
            Q0=makeQuery(id+"F1.opExtrude","CAP_EDGE",EDGE,{"disambiguationData":[OSD([sQuery(id+"F0.wireOp",EDGE,"E63")])],"isStart":false});
            var Q1;
            Q1=makeQuery(id+"F1.opExtrude","CAP_EDGE",EDGE,{"disambiguationData":[OSD([sQuery(id+"F0.wireOp",EDGE,"E64")])],"isStart":false});
            var Q2;
            Q2=makeQuery(id+"F1.opExtrude","CAP_EDGE",EDGE,{"disambiguationData":[OSD([sQuery(id+"F0.wireOp",EDGE,"E62")])],"isStart":false});
            fillet(context, id + "F2", {"entities" : qUnion([Q0, Q1, Q2]), "radius" : 9 * mm, "tangentPropagation" : true, "allowEdgeOverflow" : false});
        }
        {
            var Q0;
            Q0=makeQuery(id+"F1.opExtrude","CAP_FACE",FACE,{"disambiguationData":[OSD([sQuery(id+"F0.wireOp",EDGE,"E7"),sQuery(id+"F0.wireOp",EDGE,"E56"),sQuery(id+"F0.wireOp",EDGE,"E57"),sQuery(id+"F0.wireOp",EDGE,"E58"),sQuery(id+"F0.wireOp",EDGE,"E59"),sQuery(id+"F0.wireOp",EDGE,"E60"),sQuery(id+"F0.wireOp",EDGE,"E61"),sQuery(id+"F0.wireOp",EDGE,"E62"),sQuery(id+"F0.wireOp",EDGE,"E63"),sQuery(id+"F0.wireOp",EDGE,"E64")])],"isStart":false});
            var sketch = newSketch(context, id + "F3", { "sketchPlane" : qUnion([Q0])});
            skSolve(sketch);
        }
        {
            var Q0;
            Q0 = qSketchRegion(id + "F3", true);
            var Q1;
            {var subQ8=sQuery(id+"F0.wireOp",EDGE,"E56");Q1=makeQuery(id+"F3.imprint","IMPRINT",FACE,{"disambiguationData":[TD([[makeQuery(id+"F3.imprint","IMPRINT",EDGE,{"derivedFrom":makeQuery(id+"F1.opExtrude","CAP_EDGE",EDGE,{"disambiguationData":[OSD([subQ8])],"isStart":false})}),1.0]])]});}
            extrude(context, id + "F4", {"entities" : qUnion([Q0, Q1]), "operationType" : NewBodyOperationType.REMOVE, "oppositeDirection" : true, "depth" : 1.5 * mm, "offsetDistance" : 25 * mm});
        }
        {
            var Q0;
            {var subQ0=sQuery(id+"F0.wireOp",EDGE,"E64");var subQ1=sQuery(id+"F0.wireOp",EDGE,"E63");var subQ2=sQuery(id+"F0.wireOp",EDGE,"E62");var subQ3=sQuery(id+"F0.wireOp",EDGE,"E61");var subQ4=sQuery(id+"F0.wireOp",EDGE,"E60");var subQ5=sQuery(id+"F0.wireOp",EDGE,"E59");var subQ6=sQuery(id+"F0.wireOp",EDGE,"E58");var subQ7=sQuery(id+"F0.wireOp",EDGE,"E57");var subQ8=sQuery(id+"F0.wireOp",EDGE,"E56");var subQ9=sQuery(id+"F0.wireOp",EDGE,"E7");var subQ10=makeQuery(id+"F2.opFillet","BLEND_EDGE",EDGE,{"blendedFrom":[makeQuery(id+"F1.opExtrude","CAP_EDGE",EDGE,{"disambiguationData":[OSD([subQ0])],"isStart":false}),makeQuery(id+"F1.opExtrude","CAP_FACE",FACE,{"disambiguationData":[OSD([subQ9,subQ8,subQ7,subQ6,subQ5,subQ4,subQ3,subQ2,subQ1,subQ0])],"isStart":false})],"blendedInto":[makeQuery(id+"F1.opExtrude","CAP_FACE",FACE,{"disambiguationData":[OSD([subQ9,subQ8,subQ7,subQ6,subQ5,subQ4,subQ3,subQ2,subQ1,subQ0])],"isStart":false})]});Q0=makeQuery(id+"F4.boolean.opBoolean","MERGE",EDGE,{"derivedFrom":[subQ10,makeQuery(id+"F4.opExtrude","CAP_EDGE",EDGE,{"disambiguationData":[OSD([subQ9,subQ8,subQ7,subQ6,subQ5,subQ4,subQ3,subQ2,subQ1,subQ0]),TDD([makeQuery(id+"F3.imprint","IMPRINT",EDGE,{"derivedFrom":subQ10})])],"isStart":true})]});}
            var Q1;
            {var subQ0=sQuery(id+"F0.wireOp",EDGE,"E64");var subQ1=sQuery(id+"F0.wireOp",EDGE,"E63");var subQ2=sQuery(id+"F0.wireOp",EDGE,"E62");var subQ3=sQuery(id+"F0.wireOp",EDGE,"E61");var subQ4=sQuery(id+"F0.wireOp",EDGE,"E60");var subQ5=sQuery(id+"F0.wireOp",EDGE,"E59");var subQ6=sQuery(id+"F0.wireOp",EDGE,"E58");var subQ7=sQuery(id+"F0.wireOp",EDGE,"E57");var subQ8=sQuery(id+"F0.wireOp",EDGE,"E56");var subQ9=sQuery(id+"F0.wireOp",EDGE,"E7");var subQ10=makeQuery(id+"F2.opFillet","BLEND_EDGE",EDGE,{"blendedFrom":[makeQuery(id+"F1.opExtrude","CAP_EDGE",EDGE,{"disambiguationData":[OSD([subQ2])],"isStart":false}),makeQuery(id+"F1.opExtrude","CAP_FACE",FACE,{"disambiguationData":[OSD([subQ9,subQ8,subQ7,subQ6,subQ5,subQ4,subQ3,subQ2,subQ1,subQ0])],"isStart":false})],"blendedInto":[makeQuery(id+"F1.opExtrude","CAP_FACE",FACE,{"disambiguationData":[OSD([subQ9,subQ8,subQ7,subQ6,subQ5,subQ4,subQ3,subQ2,subQ1,subQ0])],"isStart":false})]});Q1=makeQuery(id+"F4.boolean.opBoolean","MERGE",EDGE,{"derivedFrom":[subQ10,makeQuery(id+"F4.opExtrude","CAP_EDGE",EDGE,{"disambiguationData":[OSD([subQ9,subQ8,subQ7,subQ6,subQ5,subQ4,subQ3,subQ2,subQ1,subQ0]),TDD([makeQuery(id+"F3.imprint","IMPRINT",EDGE,{"derivedFrom":subQ10})])],"isStart":true})]});}
            var Q2;
            {var subQ0=sQuery(id+"F0.wireOp",EDGE,"E64");var subQ1=sQuery(id+"F0.wireOp",EDGE,"E63");var subQ2=sQuery(id+"F0.wireOp",EDGE,"E62");var subQ3=sQuery(id+"F0.wireOp",EDGE,"E61");var subQ4=sQuery(id+"F0.wireOp",EDGE,"E60");var subQ5=sQuery(id+"F0.wireOp",EDGE,"E59");var subQ6=sQuery(id+"F0.wireOp",EDGE,"E58");var subQ7=sQuery(id+"F0.wireOp",EDGE,"E57");var subQ8=sQuery(id+"F0.wireOp",EDGE,"E56");var subQ9=sQuery(id+"F0.wireOp",EDGE,"E7");var subQ10=makeQuery(id+"F2.opFillet","BLEND_EDGE",EDGE,{"blendedFrom":[makeQuery(id+"F1.opExtrude","CAP_EDGE",EDGE,{"disambiguationData":[OSD([subQ1])],"isStart":false}),makeQuery(id+"F1.opExtrude","CAP_FACE",FACE,{"disambiguationData":[OSD([subQ9,subQ8,subQ7,subQ6,subQ5,subQ4,subQ3,subQ2,subQ1,subQ0])],"isStart":false})],"blendedInto":[makeQuery(id+"F1.opExtrude","CAP_FACE",FACE,{"disambiguationData":[OSD([subQ9,subQ8,subQ7,subQ6,subQ5,subQ4,subQ3,subQ2,subQ1,subQ0])],"isStart":false})]});Q2=makeQuery(id+"F4.boolean.opBoolean","MERGE",EDGE,{"derivedFrom":[subQ10,makeQuery(id+"F4.opExtrude","CAP_EDGE",EDGE,{"disambiguationData":[OSD([subQ9,subQ8,subQ7,subQ6,subQ5,subQ4,subQ3,subQ2,subQ1,subQ0]),TDD([makeQuery(id+"F3.imprint","IMPRINT",EDGE,{"derivedFrom":subQ10})])],"isStart":true})]});}
            var Q3;
            {var subQ0=sQuery(id+"F0.wireOp",EDGE,"E63");Q3=makeQuery(id+"F2.opFillet","BLEND_EDGE",EDGE,{"blendedFrom":[makeQuery(id+"F1.opExtrude","CAP_EDGE",EDGE,{"disambiguationData":[OSD([subQ0])],"isStart":false}),makeQuery(id+"F1.opExtrude","CAP_FACE",FACE,{"disambiguationData":[OSD([sQuery(id+"F0.wireOp",EDGE,"E7"),sQuery(id+"F0.wireOp",EDGE,"E56"),sQuery(id+"F0.wireOp",EDGE,"E57"),sQuery(id+"F0.wireOp",EDGE,"E58"),sQuery(id+"F0.wireOp",EDGE,"E59"),sQuery(id+"F0.wireOp",EDGE,"E60"),sQuery(id+"F0.wireOp",EDGE,"E61"),sQuery(id+"F0.wireOp",EDGE,"E62"),subQ0,sQuery(id+"F0.wireOp",EDGE,"E64"),sQuery(id+"F0.wireOp",EDGE,"E65"),sQuery(id+"F0.wireOp",EDGE,"E68"),sQuery(id+"F0.wireOp",EDGE,"E69"),sQuery(id+"F0.wireOp",EDGE,"E70"),sQuery(id+"F0.wireOp",EDGE,"E71"),sQuery(id+"F0.wireOp",EDGE,"E72"),sQuery(id+"F0.wireOp",EDGE,"E74")])],"isStart":true})],"blendedInto":[makeQuery(id+"F1.opExtrude","CAP_FACE",FACE,{"disambiguationData":[OSD([sQuery(id+"F0.wireOp",EDGE,"E7"),sQuery(id+"F0.wireOp",EDGE,"E56"),sQuery(id+"F0.wireOp",EDGE,"E57"),sQuery(id+"F0.wireOp",EDGE,"E58"),sQuery(id+"F0.wireOp",EDGE,"E59"),sQuery(id+"F0.wireOp",EDGE,"E60"),sQuery(id+"F0.wireOp",EDGE,"E61"),sQuery(id+"F0.wireOp",EDGE,"E62"),subQ0,sQuery(id+"F0.wireOp",EDGE,"E64"),sQuery(id+"F0.wireOp",EDGE,"E65"),sQuery(id+"F0.wireOp",EDGE,"E68"),sQuery(id+"F0.wireOp",EDGE,"E69"),sQuery(id+"F0.wireOp",EDGE,"E70"),sQuery(id+"F0.wireOp",EDGE,"E71"),sQuery(id+"F0.wireOp",EDGE,"E72"),sQuery(id+"F0.wireOp",EDGE,"E74")])],"isStart":true})]});}
            var Q4;
            {var subQ0=sQuery(id+"F0.wireOp",EDGE,"E64");Q4=makeQuery(id+"F2.opFillet","BLEND_EDGE",EDGE,{"blendedFrom":[makeQuery(id+"F1.opExtrude","CAP_EDGE",EDGE,{"disambiguationData":[OSD([subQ0])],"isStart":false}),makeQuery(id+"F1.opExtrude","CAP_FACE",FACE,{"disambiguationData":[OSD([sQuery(id+"F0.wireOp",EDGE,"E7"),sQuery(id+"F0.wireOp",EDGE,"E56"),sQuery(id+"F0.wireOp",EDGE,"E57"),sQuery(id+"F0.wireOp",EDGE,"E58"),sQuery(id+"F0.wireOp",EDGE,"E59"),sQuery(id+"F0.wireOp",EDGE,"E60"),sQuery(id+"F0.wireOp",EDGE,"E61"),sQuery(id+"F0.wireOp",EDGE,"E62"),sQuery(id+"F0.wireOp",EDGE,"E63"),subQ0,sQuery(id+"F0.wireOp",EDGE,"E65"),sQuery(id+"F0.wireOp",EDGE,"E68"),sQuery(id+"F0.wireOp",EDGE,"E69"),sQuery(id+"F0.wireOp",EDGE,"E70"),sQuery(id+"F0.wireOp",EDGE,"E71"),sQuery(id+"F0.wireOp",EDGE,"E72"),sQuery(id+"F0.wireOp",EDGE,"E74")])],"isStart":true})],"blendedInto":[makeQuery(id+"F1.opExtrude","CAP_FACE",FACE,{"disambiguationData":[OSD([sQuery(id+"F0.wireOp",EDGE,"E7"),sQuery(id+"F0.wireOp",EDGE,"E56"),sQuery(id+"F0.wireOp",EDGE,"E57"),sQuery(id+"F0.wireOp",EDGE,"E58"),sQuery(id+"F0.wireOp",EDGE,"E59"),sQuery(id+"F0.wireOp",EDGE,"E60"),sQuery(id+"F0.wireOp",EDGE,"E61"),sQuery(id+"F0.wireOp",EDGE,"E62"),sQuery(id+"F0.wireOp",EDGE,"E63"),subQ0,sQuery(id+"F0.wireOp",EDGE,"E65"),sQuery(id+"F0.wireOp",EDGE,"E68"),sQuery(id+"F0.wireOp",EDGE,"E69"),sQuery(id+"F0.wireOp",EDGE,"E70"),sQuery(id+"F0.wireOp",EDGE,"E71"),sQuery(id+"F0.wireOp",EDGE,"E72"),sQuery(id+"F0.wireOp",EDGE,"E74")])],"isStart":true})]});}
            var Q5;
            {var subQ0=sQuery(id+"F0.wireOp",EDGE,"E62");Q5=makeQuery(id+"F2.opFillet","BLEND_EDGE",EDGE,{"blendedFrom":[makeQuery(id+"F1.opExtrude","CAP_EDGE",EDGE,{"disambiguationData":[OSD([subQ0])],"isStart":false}),makeQuery(id+"F1.opExtrude","CAP_FACE",FACE,{"disambiguationData":[OSD([sQuery(id+"F0.wireOp",EDGE,"E7"),sQuery(id+"F0.wireOp",EDGE,"E56"),sQuery(id+"F0.wireOp",EDGE,"E57"),sQuery(id+"F0.wireOp",EDGE,"E58"),sQuery(id+"F0.wireOp",EDGE,"E59"),sQuery(id+"F0.wireOp",EDGE,"E60"),sQuery(id+"F0.wireOp",EDGE,"E61"),subQ0,sQuery(id+"F0.wireOp",EDGE,"E63"),sQuery(id+"F0.wireOp",EDGE,"E64"),sQuery(id+"F0.wireOp",EDGE,"E65"),sQuery(id+"F0.wireOp",EDGE,"E68"),sQuery(id+"F0.wireOp",EDGE,"E69"),sQuery(id+"F0.wireOp",EDGE,"E70"),sQuery(id+"F0.wireOp",EDGE,"E71"),sQuery(id+"F0.wireOp",EDGE,"E72"),sQuery(id+"F0.wireOp",EDGE,"E74")])],"isStart":true})],"blendedInto":[makeQuery(id+"F1.opExtrude","CAP_FACE",FACE,{"disambiguationData":[OSD([sQuery(id+"F0.wireOp",EDGE,"E7"),sQuery(id+"F0.wireOp",EDGE,"E56"),sQuery(id+"F0.wireOp",EDGE,"E57"),sQuery(id+"F0.wireOp",EDGE,"E58"),sQuery(id+"F0.wireOp",EDGE,"E59"),sQuery(id+"F0.wireOp",EDGE,"E60"),sQuery(id+"F0.wireOp",EDGE,"E61"),subQ0,sQuery(id+"F0.wireOp",EDGE,"E63"),sQuery(id+"F0.wireOp",EDGE,"E64"),sQuery(id+"F0.wireOp",EDGE,"E65"),sQuery(id+"F0.wireOp",EDGE,"E68"),sQuery(id+"F0.wireOp",EDGE,"E69"),sQuery(id+"F0.wireOp",EDGE,"E70"),sQuery(id+"F0.wireOp",EDGE,"E71"),sQuery(id+"F0.wireOp",EDGE,"E72"),sQuery(id+"F0.wireOp",EDGE,"E74")])],"isStart":true})]});}
            fillet(context, id + "F5", {"entities" : qUnion([Q0, Q1, Q2, Q3, Q4, Q5]), "radius" : 3 * mm, "tangentPropagation" : true, "allowEdgeOverflow" : false});
        }
        {
            var Q0;
            Q0=makeQuery(id+"F1.opExtrude","SWEPT_EDGE",EDGE,{"disambiguationData":[OSD([sQuery(id+"F0.wireOp",EDGE,"E60"),sQuery(id+"F0.wireOp",EDGE,"E68")])]});
            var Q1;
            Q1=makeQuery(id+"F1.opExtrude","SWEPT_EDGE",EDGE,{"disambiguationData":[OSD([sQuery(id+"F0.wireOp",EDGE,"E61"),sQuery(id+"F0.wireOp",EDGE,"E69")])]});
            var Q2;
            Q2=makeQuery(id+"F1.opExtrude","SWEPT_EDGE",EDGE,{"disambiguationData":[OSD([sQuery(id+"F0.wireOp",EDGE,"E58"),sQuery(id+"F0.wireOp",EDGE,"E74")])]});
            var Q3;
            Q3=makeQuery(id+"F1.opExtrude","SWEPT_EDGE",EDGE,{"disambiguationData":[OSD([sQuery(id+"F0.wireOp",EDGE,"E59"),sQuery(id+"F0.wireOp",EDGE,"E72")])]});
            var Q4;
            Q4=makeQuery(id+"F1.opExtrude","SWEPT_EDGE",EDGE,{"disambiguationData":[OSD([sQuery(id+"F0.wireOp",EDGE,"E56"),sQuery(id+"F0.wireOp",EDGE,"E71")])]});
            var Q5;
            Q5=makeQuery(id+"F1.opExtrude","SWEPT_EDGE",EDGE,{"disambiguationData":[OSD([sQuery(id+"F0.wireOp",EDGE,"E57"),sQuery(id+"F0.wireOp",EDGE,"E70")])]});
            fillet(context, id + "F6", {"entities" : qUnion([Q0, Q1, Q2, Q3, Q4, Q5]), "radius" : 7 * mm, "tangentPropagation" : true, "allowEdgeOverflow" : false});
        }
    });
